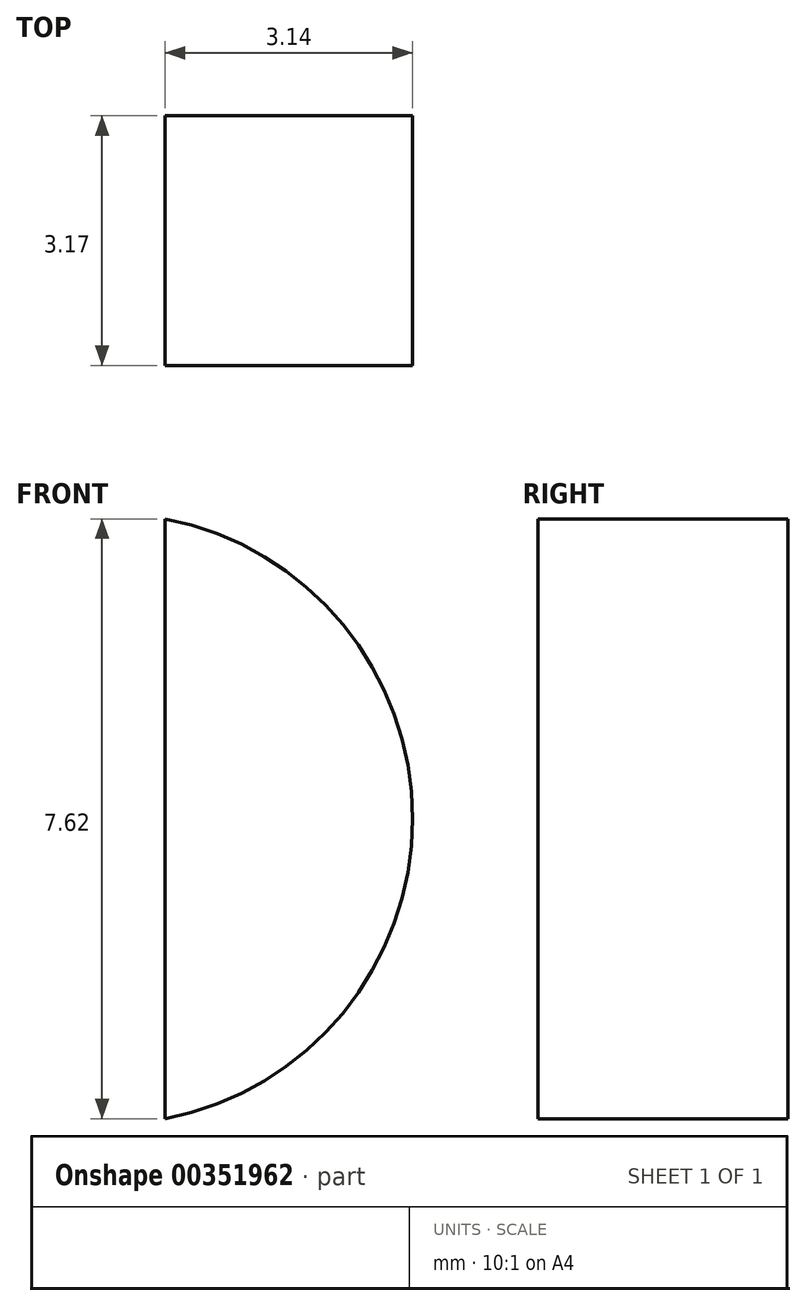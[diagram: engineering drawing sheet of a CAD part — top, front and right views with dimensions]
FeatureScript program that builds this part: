
annotation { "Feature Type Name" : "Feature", "Feature Type Description" : "" }
export const myFeature = defineFeature(function(context is Context, id is Id, definition is map)
    precondition{}
    {
        {
            var Q0;
            Q0=qCreatedBy(makeId("Front.planeOp"),FACE);
            var sketch = newSketch(context, id + "F0", { "sketchPlane" : qUnion([Q0])});
            skLineSegment(sketch, "E0", {"start": v(0, 7.62) * mm, "end": v(0, 0) * mm});
            skArc(sketch, "E1", {"start": v(0, 0) * mm, "mid": v(3.14, 3.81) * mm, "end": v(0, 7.62) * mm});
            skSolve(sketch);
        }
        {
            var Q0;
            Q0 = qSketchRegion(id + "F0", true);
            extrude(context, id + "F1", {"entities" : qUnion([Q0]), "depth" : 3.17 * mm});
        }
    });
